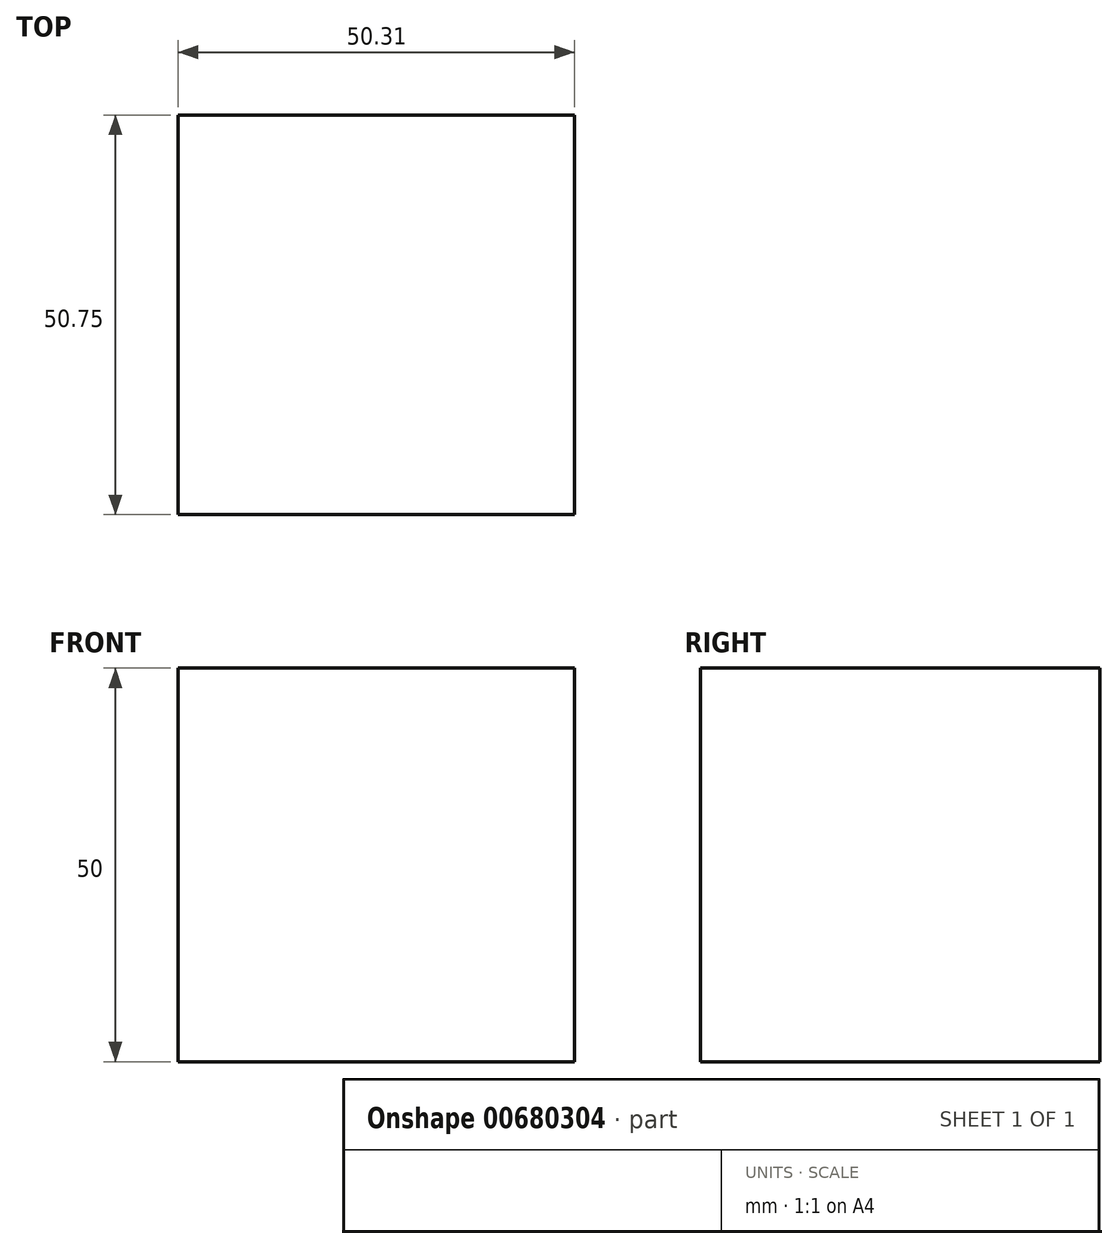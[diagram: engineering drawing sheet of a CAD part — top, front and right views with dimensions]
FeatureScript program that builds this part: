
annotation { "Feature Type Name" : "Feature", "Feature Type Description" : "" }
export const myFeature = defineFeature(function(context is Context, id is Id, definition is map)
    precondition{}
    {
        {
            var Q0;
            Q0=qCreatedBy(makeId("Top.planeOp"),FACE);
            var sketch = newSketch(context, id + "F0", { "sketchPlane" : qUnion([Q0])});
            skLineSegment(sketch, "E0.bottom", {"start": v(0, 0) * mm, "end": v(-50.31, 0) * mm});
            skLineSegment(sketch, "E0.top", {"start": v(0, 50.75) * mm, "end": v(-50.31, 50.75) * mm});
            skLineSegment(sketch, "E0.left", {"start": v(0, 0) * mm, "end": v(0, 50.75) * mm});
            skLineSegment(sketch, "E0.right", {"start": v(-50.31, 0) * mm, "end": v(-50.31, 50.75) * mm});
            skSolve(sketch);
        }
        {
            var Q0;
            Q0 = qSketchRegion(id + "F0", true);
            extrude(context, id + "F1", {"entities" : qUnion([Q0]), "depth" : 50 * mm, "offsetDistance" : 25 * mm});
        }
    });
